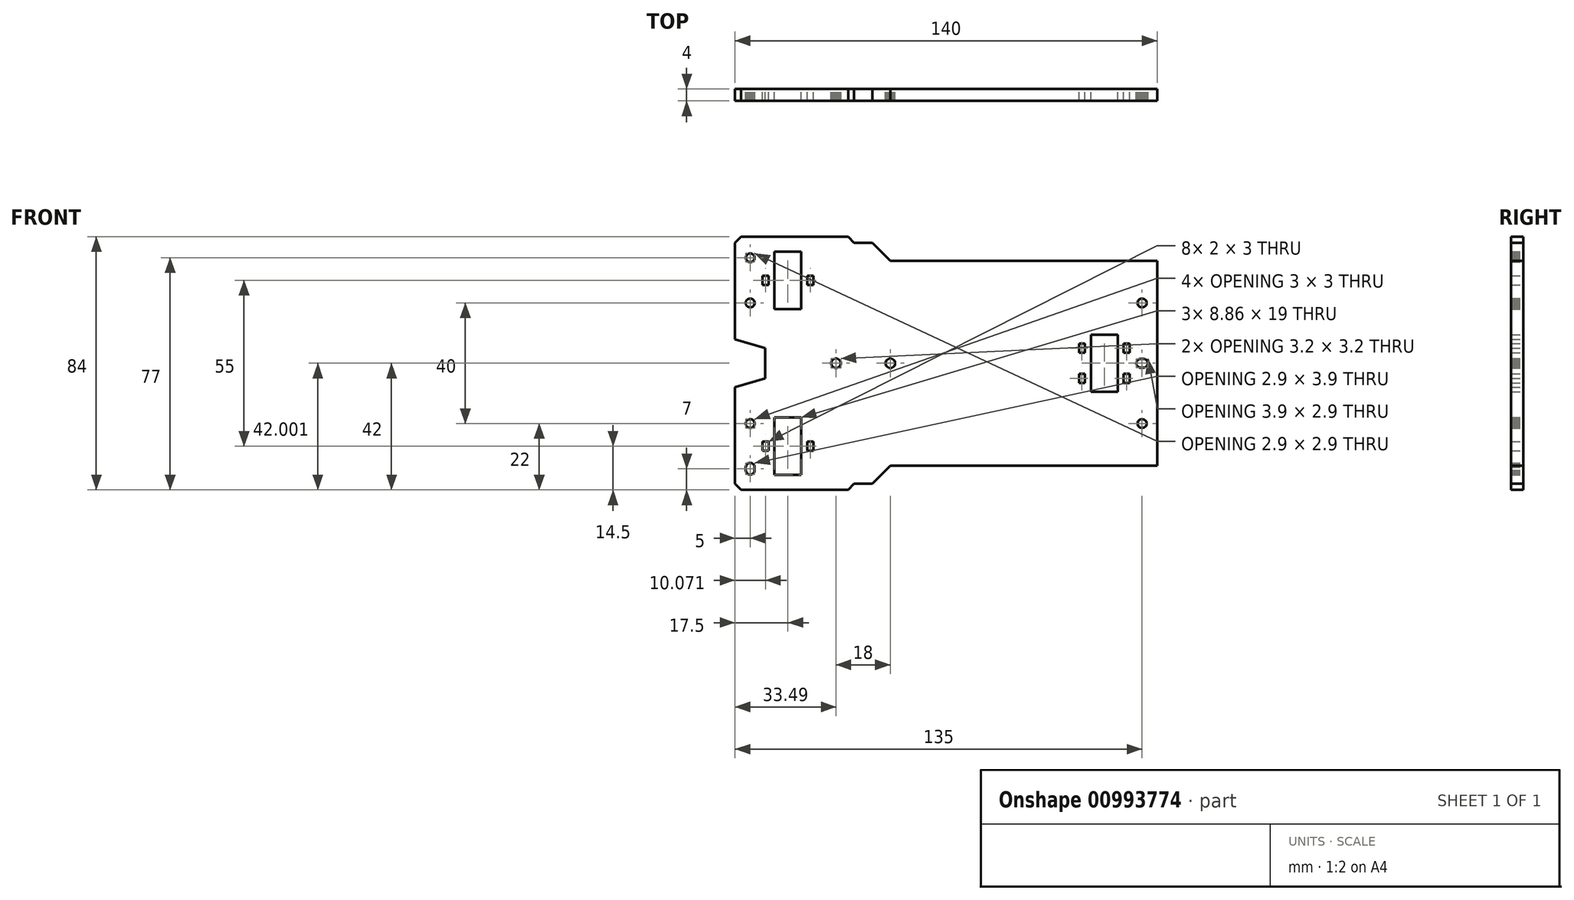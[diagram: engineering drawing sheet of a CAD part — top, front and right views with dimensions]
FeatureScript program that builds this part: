
annotation { "Feature Type Name" : "Feature", "Feature Type Description" : "" }
export const myFeature = defineFeature(function(context is Context, id is Id, definition is map)
    precondition{}
    {
        {
            var Q0;
            Q0=qCreatedBy(makeId("Front.planeOp"),FACE);
            var sketch = newSketch(context, id + "F0", { "sketchPlane" : qUnion([Q0])});
            skLineSegment(sketch, "E0", {"start": v(-65, -33.05) * mm, "end": v(-64.62, -33.1) * mm});
            skLineSegment(sketch, "E1", {"start": v(-64.62, -33.1) * mm, "end": v(-64.28, -33.24) * mm});
            skLineSegment(sketch, "E2", {"start": v(-66.26, -33.77) * mm, "end": v(-66.03, -33.47) * mm});
            skLineSegment(sketch, "E3", {"start": v(-66.03, -33.47) * mm, "end": v(-65.73, -33.24) * mm});
            skLineSegment(sketch, "E4", {"start": v(-66.45, -35.5) * mm, "end": v(-66.45, -34.5) * mm});
            skLineSegment(sketch, "E5", {"start": v(-66.45, -34.5) * mm, "end": v(-66.4, -34.12) * mm});
            skLineSegment(sketch, "E6", {"start": v(-66.4, -34.12) * mm, "end": v(-66.26, -33.77) * mm});
            skLineSegment(sketch, "E7", {"start": v(-65.73, -33.24) * mm, "end": v(-65.38, -33.1) * mm});
            skLineSegment(sketch, "E8", {"start": v(-65.38, -33.1) * mm, "end": v(-65, -33.05) * mm});
            skLineSegment(sketch, "E9", {"start": v(-63.97, -33.47) * mm, "end": v(-63.74, -33.77) * mm});
            skLineSegment(sketch, "E10", {"start": v(63.77, -1.26) * mm, "end": v(63.47, -1.03) * mm});
            skLineSegment(sketch, "E11", {"start": v(-64.28, -33.24) * mm, "end": v(-63.97, -33.47) * mm});
            skLineSegment(sketch, "E12", {"start": v(63.47, -1.03) * mm, "end": v(63.24, -0.73) * mm});
            skLineSegment(sketch, "E13", {"start": v(-63.74, -33.77) * mm, "end": v(-63.6, -34.12) * mm});
            skLineSegment(sketch, "E14", {"start": v(64.5, -1.45) * mm, "end": v(64.12, -1.4) * mm});
            skLineSegment(sketch, "E15", {"start": v(-63.55, -35.5) * mm, "end": v(-63.55, -34.5) * mm});
            skLineSegment(sketch, "E16", {"start": v(-63.6, -34.12) * mm, "end": v(-63.55, -34.5) * mm});
            skLineSegment(sketch, "E17", {"start": v(65.5, -1.45) * mm, "end": v(64.5, -1.45) * mm});
            skLineSegment(sketch, "E18", {"start": v(64.12, -1.4) * mm, "end": v(63.77, -1.26) * mm});
            skLineSegment(sketch, "E19", {"start": v(63.1, -0.38) * mm, "end": v(63.05, 0) * mm});
            skLineSegment(sketch, "E20", {"start": v(63.1, 0.38) * mm, "end": v(63.24, 0.72) * mm});
            skLineSegment(sketch, "E21", {"start": v(63.77, 1.26) * mm, "end": v(64.12, 1.4) * mm});
            skLineSegment(sketch, "E22", {"start": v(64.12, 1.4) * mm, "end": v(64.5, 1.45) * mm});
            skLineSegment(sketch, "E23", {"start": v(65.5, 1.45) * mm, "end": v(64.5, 1.45) * mm});
            skLineSegment(sketch, "E24", {"start": v(63.24, 0.72) * mm, "end": v(63.47, 1.03) * mm});
            skLineSegment(sketch, "E25", {"start": v(63.47, 1.03) * mm, "end": v(63.77, 1.26) * mm});
            skLineSegment(sketch, "E26", {"start": v(63.24, -0.73) * mm, "end": v(63.1, -0.38) * mm});
            skLineSegment(sketch, "E27", {"start": v(63.05, 0) * mm, "end": v(63.1, 0.38) * mm});
            skLineSegment(sketch, "E28", {"start": v(46.07, -6.5) * mm, "end": v(44.07, -6.5) * mm});
            skLineSegment(sketch, "E29", {"start": v(44.07, -6.5) * mm, "end": v(44.07, -3.5) * mm});
            skLineSegment(sketch, "E30", {"start": v(-20.06, 0.41) * mm, "end": v(-20.1, 0) * mm});
            skLineSegment(sketch, "E31", {"start": v(-19.64, 1.13) * mm, "end": v(-19.9, 0.8) * mm});
            skLineSegment(sketch, "E32", {"start": v(-19.3, 1.39) * mm, "end": v(-19.64, 1.13) * mm});
            skLineSegment(sketch, "E33", {"start": v(48.07, -9.5) * mm, "end": v(48.07, 9.5) * mm});
            skLineSegment(sketch, "E34", {"start": v(44.07, -3.5) * mm, "end": v(46.07, -3.5) * mm});
            skLineSegment(sketch, "E35", {"start": v(58.93, -6.5) * mm, "end": v(60.93, -6.5) * mm});
            skLineSegment(sketch, "E36", {"start": v(46.07, -3.5) * mm, "end": v(46.07, -6.5) * mm});
            skLineSegment(sketch, "E37", {"start": v(56.93, -9.5) * mm, "end": v(48.07, -9.5) * mm});
            skLineSegment(sketch, "E38", {"start": v(-18.92, 1.55) * mm, "end": v(-19.3, 1.39) * mm});
            skLineSegment(sketch, "E39", {"start": v(-20.1, 0) * mm, "end": v(-20.06, -0.41) * mm});
            skLineSegment(sketch, "E40", {"start": v(60.93, -6.5) * mm, "end": v(60.93, -3.5) * mm});
            skLineSegment(sketch, "E41", {"start": v(56.93, 9.5) * mm, "end": v(56.93, -9.5) * mm});
            skLineSegment(sketch, "E42", {"start": v(48.07, 9.5) * mm, "end": v(56.93, 9.5) * mm});
            skLineSegment(sketch, "E43", {"start": v(-20.06, -0.41) * mm, "end": v(-19.9, -0.8) * mm});
            skLineSegment(sketch, "E44", {"start": v(-19.9, 0.8) * mm, "end": v(-20.06, 0.41) * mm});
            skLineSegment(sketch, "E45", {"start": v(-16.96, -0.41) * mm, "end": v(-16.9, 0) * mm});
            skLineSegment(sketch, "E46", {"start": v(-17.7, -1.38) * mm, "end": v(-17.38, -1.13) * mm});
            skLineSegment(sketch, "E47", {"start": v(-18.1, -1.54) * mm, "end": v(-17.7, -1.38) * mm});
            skLineSegment(sketch, "E48", {"start": v(-18.5, -1.6) * mm, "end": v(-18.1, -1.54) * mm});
            skLineSegment(sketch, "E49", {"start": v(-18.92, -1.54) * mm, "end": v(-18.5, -1.6) * mm});
            skLineSegment(sketch, "E50", {"start": v(-16.96, 0.41) * mm, "end": v(-17.12, 0.8) * mm});
            skLineSegment(sketch, "E51", {"start": v(-18.5, 1.6) * mm, "end": v(-18.92, 1.55) * mm});
            skLineSegment(sketch, "E52", {"start": v(-17.7, 1.39) * mm, "end": v(-18.1, 1.55) * mm});
            skLineSegment(sketch, "E53", {"start": v(-17.38, 1.13) * mm, "end": v(-17.7, 1.39) * mm});
            skLineSegment(sketch, "E54", {"start": v(-16.9, 0) * mm, "end": v(-16.96, 0.41) * mm});
            skLineSegment(sketch, "E55", {"start": v(-19.3, -1.38) * mm, "end": v(-18.92, -1.54) * mm});
            skLineSegment(sketch, "E56", {"start": v(-18.1, 1.55) * mm, "end": v(-18.5, 1.6) * mm});
            skLineSegment(sketch, "E57", {"start": v(-19.64, -1.13) * mm, "end": v(-19.3, -1.38) * mm});
            skLineSegment(sketch, "E58", {"start": v(-17.12, 0.8) * mm, "end": v(-17.38, 1.13) * mm});
            skLineSegment(sketch, "E59", {"start": v(-17.38, -1.13) * mm, "end": v(-17.12, -0.8) * mm});
            skLineSegment(sketch, "E60", {"start": v(-17.12, -0.8) * mm, "end": v(-16.96, -0.41) * mm});
            skLineSegment(sketch, "E61", {"start": v(-35.38, 1.13) * mm, "end": v(-35.7, 1.39) * mm});
            skLineSegment(sketch, "E62", {"start": v(-38.06, 0.41) * mm, "end": v(-38.1, 0) * mm});
            skLineSegment(sketch, "E63", {"start": v(-37.64, -1.13) * mm, "end": v(-37.3, -1.38) * mm});
            skLineSegment(sketch, "E64", {"start": v(-35.12, 0.8) * mm, "end": v(-35.38, 1.13) * mm});
            skLineSegment(sketch, "E65", {"start": v(-38.1, 0) * mm, "end": v(-38.06, -0.41) * mm});
            skLineSegment(sketch, "E66", {"start": v(-37.9, 0.8) * mm, "end": v(-38.06, 0.41) * mm});
            skLineSegment(sketch, "E67", {"start": v(-37.3, 1.39) * mm, "end": v(-37.64, 1.13) * mm});
            skLineSegment(sketch, "E68", {"start": v(-36.1, 1.55) * mm, "end": v(-36.5, 1.6) * mm});
            skLineSegment(sketch, "E69", {"start": v(-37.64, 1.13) * mm, "end": v(-37.9, 0.8) * mm});
            skLineSegment(sketch, "E70", {"start": v(-37.9, -0.8) * mm, "end": v(-37.64, -1.13) * mm});
            skLineSegment(sketch, "E71", {"start": v(-38.06, -0.41) * mm, "end": v(-37.9, -0.8) * mm});
            skLineSegment(sketch, "E72", {"start": v(-37.3, -1.38) * mm, "end": v(-36.92, -1.54) * mm});
            skLineSegment(sketch, "E73", {"start": v(-36.5, 1.6) * mm, "end": v(-36.92, 1.55) * mm});
            skLineSegment(sketch, "E74", {"start": v(-36.92, 1.55) * mm, "end": v(-37.3, 1.39) * mm});
            skLineSegment(sketch, "E75", {"start": v(-35.7, 1.39) * mm, "end": v(-36.1, 1.55) * mm});
            skLineSegment(sketch, "E76", {"start": v(-19.9, -0.8) * mm, "end": v(-19.64, -1.13) * mm});
            skLineSegment(sketch, "E77", {"start": v(-35.7, -1.38) * mm, "end": v(-35.38, -1.13) * mm});
            skLineSegment(sketch, "E78", {"start": v(-56.93, -37) * mm, "end": v(-48.07, -37) * mm});
            skLineSegment(sketch, "E79", {"start": v(-48.07, 18) * mm, "end": v(-56.93, 18) * mm});
            skLineSegment(sketch, "E80", {"start": v(-56.93, 18) * mm, "end": v(-56.93, 37) * mm});
            skLineSegment(sketch, "E81", {"start": v(-48.07, 37) * mm, "end": v(-48.07, 18) * mm});
            skLineSegment(sketch, "E82", {"start": v(-35.12, -0.8) * mm, "end": v(-34.96, -0.41) * mm});
            skLineSegment(sketch, "E83", {"start": v(-34.96, -0.41) * mm, "end": v(-34.9, 0) * mm});
            skLineSegment(sketch, "E84", {"start": v(-36.1, -1.54) * mm, "end": v(-35.7, -1.38) * mm});
            skLineSegment(sketch, "E85", {"start": v(-34.9, 0) * mm, "end": v(-34.96, 0.41) * mm});
            skLineSegment(sketch, "E86", {"start": v(-35.38, -1.13) * mm, "end": v(-35.12, -0.8) * mm});
            skLineSegment(sketch, "E87", {"start": v(-56.93, -18) * mm, "end": v(-56.93, -37) * mm});
            skLineSegment(sketch, "E88", {"start": v(-48.07, -37) * mm, "end": v(-48.07, -18) * mm});
            skLineSegment(sketch, "E89", {"start": v(-36.5, -1.6) * mm, "end": v(-36.1, -1.54) * mm});
            skLineSegment(sketch, "E90", {"start": v(-36.92, -1.54) * mm, "end": v(-36.5, -1.6) * mm});
            skLineSegment(sketch, "E91", {"start": v(-48.07, -18) * mm, "end": v(-56.93, -18) * mm});
            skLineSegment(sketch, "E92", {"start": v(-34.96, 0.41) * mm, "end": v(-35.12, 0.8) * mm});
            skLineSegment(sketch, "E93", {"start": v(-44.07, -29) * mm, "end": v(-44.07, -26) * mm});
            skLineSegment(sketch, "E94", {"start": v(-46.07, -26) * mm, "end": v(-46.07, -29) * mm});
            skLineSegment(sketch, "E95", {"start": v(-46.07, -29) * mm, "end": v(-44.07, -29) * mm});
            skLineSegment(sketch, "E96", {"start": v(-58.93, 26) * mm, "end": v(-60.93, 26) * mm});
            skLineSegment(sketch, "E97", {"start": v(-60.93, 26) * mm, "end": v(-60.93, 29) * mm});
            skLineSegment(sketch, "E98", {"start": v(-44.07, -26) * mm, "end": v(-46.07, -26) * mm});
            skLineSegment(sketch, "E99", {"start": v(-58.93, -29) * mm, "end": v(-60.93, -29) * mm});
            skLineSegment(sketch, "E100", {"start": v(-60.93, -29) * mm, "end": v(-60.93, -26) * mm});
            skLineSegment(sketch, "E101", {"start": v(-44.07, 26) * mm, "end": v(-44.07, 29) * mm});
            skLineSegment(sketch, "E102", {"start": v(-46.07, 29) * mm, "end": v(-46.07, 26) * mm});
            skLineSegment(sketch, "E103", {"start": v(-60.93, -26) * mm, "end": v(-58.93, -26) * mm});
            skLineSegment(sketch, "E104", {"start": v(-58.93, -26) * mm, "end": v(-58.93, -29) * mm});
            skLineSegment(sketch, "E105", {"start": v(-44.07, 29) * mm, "end": v(-46.07, 29) * mm});
            skLineSegment(sketch, "E106", {"start": v(-46.07, 26) * mm, "end": v(-44.07, 26) * mm});
            skLineSegment(sketch, "E107", {"start": v(-58.93, 29) * mm, "end": v(-58.93, 26) * mm});
            skLineSegment(sketch, "E108", {"start": v(-56.93, 37) * mm, "end": v(-48.07, 37) * mm});
            skLineSegment(sketch, "E109", {"start": v(-30.5, 12) * mm, "end": v(-30.5, 6) * mm});
            skLineSegment(sketch, "E110", {"start": v(-30.5, -18) * mm, "end": v(-24.5, -18) * mm});
            skLineSegment(sketch, "E111", {"start": v(-30.5, 24) * mm, "end": v(-30.5, 18) * mm});
            skLineSegment(sketch, "E112", {"start": v(-24.5, 6) * mm, "end": v(-24.5, 12) * mm});
            skLineSegment(sketch, "E113", {"start": v(-24.5, -6) * mm, "end": v(-24.5, -12) * mm});
            skLineSegment(sketch, "E114", {"start": v(-24.5, 24) * mm, "end": v(-30.5, 24) * mm});
            skLineSegment(sketch, "E115", {"start": v(-30.5, 6) * mm, "end": v(-24.5, 6) * mm});
            skLineSegment(sketch, "E116", {"start": v(-24.5, 12) * mm, "end": v(-30.5, 12) * mm});
            skLineSegment(sketch, "E117", {"start": v(-30.5, -6) * mm, "end": v(-24.5, -6) * mm});
            skLineSegment(sketch, "E118", {"start": v(-24.5, -12) * mm, "end": v(-30.5, -12) * mm});
            skLineSegment(sketch, "E119", {"start": v(-30.5, 18) * mm, "end": v(-24.5, 18) * mm});
            skLineSegment(sketch, "E120", {"start": v(-60.93, 29) * mm, "end": v(-58.93, 29) * mm});
            skLineSegment(sketch, "E121", {"start": v(-24.5, -18) * mm, "end": v(-24.5, -24) * mm});
            skLineSegment(sketch, "E122", {"start": v(-24.5, 18) * mm, "end": v(-24.5, 24) * mm});
            skLineSegment(sketch, "E123", {"start": v(-30.5, -12) * mm, "end": v(-30.5, -6) * mm});
            skLineSegment(sketch, "E124", {"start": v(-24.5, -24) * mm, "end": v(-30.5, -24) * mm});
            skLineSegment(sketch, "E125", {"start": v(-30.5, -24) * mm, "end": v(-30.5, -18) * mm});
            skLineSegment(sketch, "E126", {"start": v(63.7, 20.75) * mm, "end": v(63.94, 21.06) * mm});
            skLineSegment(sketch, "E127", {"start": v(63.55, 20.39) * mm, "end": v(63.7, 20.75) * mm});
            skLineSegment(sketch, "E128", {"start": v(63.94, 21.06) * mm, "end": v(64.25, 21.3) * mm});
            skLineSegment(sketch, "E129", {"start": v(65.39, 21.45) * mm, "end": v(65.75, 21.3) * mm});
            skLineSegment(sketch, "E130", {"start": v(63.5, 20) * mm, "end": v(63.55, 20.39) * mm});
            skLineSegment(sketch, "E131", {"start": v(64.25, 21.3) * mm, "end": v(64.61, 21.45) * mm});
            skLineSegment(sketch, "E132", {"start": v(64.61, 21.45) * mm, "end": v(65, 21.5) * mm});
            skLineSegment(sketch, "E133", {"start": v(65, 21.5) * mm, "end": v(65.39, 21.45) * mm});
            skLineSegment(sketch, "E134", {"start": v(65.75, 21.3) * mm, "end": v(66.06, 21.06) * mm});
            skLineSegment(sketch, "E135", {"start": v(66.06, 21.06) * mm, "end": v(66.3, 20.75) * mm});
            skLineSegment(sketch, "E136", {"start": v(63.55, 19.61) * mm, "end": v(63.5, 20) * mm});
            skLineSegment(sketch, "E137", {"start": v(-70, 40) * mm, "end": v(-70, 8) * mm});
            skLineSegment(sketch, "E138", {"start": v(-60, 5) * mm, "end": v(-70, 8) * mm});
            skLineSegment(sketch, "E139", {"start": v(-60, -5) * mm, "end": v(-60, 5) * mm});
            skLineSegment(sketch, "E140", {"start": v(-70, -8) * mm, "end": v(-60, -5) * mm});
            skLineSegment(sketch, "E141", {"start": v(-70, -8) * mm, "end": v(-70, -40) * mm});
            skLineSegment(sketch, "E142", {"start": v(-70, -40) * mm, "end": v(-68, -42) * mm});
            skLineSegment(sketch, "E143", {"start": v(-68, -42) * mm, "end": v(-32.5, -42) * mm});
            skLineSegment(sketch, "E144", {"start": v(-30.5, -40) * mm, "end": v(-32.5, -42) * mm});
            skLineSegment(sketch, "E145", {"start": v(-30.5, -40) * mm, "end": v(-24.5, -40) * mm});
            skLineSegment(sketch, "E146", {"start": v(-24.5, -40) * mm, "end": v(-18.5, -34) * mm});
            skLineSegment(sketch, "E147", {"start": v(-18.5, -34) * mm, "end": v(70, -34) * mm});
            skLineSegment(sketch, "E148", {"start": v(70, -34) * mm, "end": v(70, 34) * mm});
            skLineSegment(sketch, "E149", {"start": v(-18.5, 34) * mm, "end": v(70, 34) * mm});
            skLineSegment(sketch, "E150", {"start": v(-24.5, 40) * mm, "end": v(-18.5, 34) * mm});
            skLineSegment(sketch, "E151", {"start": v(-24.5, 40) * mm, "end": v(-30.5, 40) * mm});
            skLineSegment(sketch, "E152", {"start": v(-30.5, 40) * mm, "end": v(-32.5, 42) * mm});
            skLineSegment(sketch, "E153", {"start": v(-32.5, 42) * mm, "end": v(-68, 42) * mm});
            skLineSegment(sketch, "E154", {"start": v(-70, 40) * mm, "end": v(-68, 42) * mm});
            skLineSegment(sketch, "E155", {"start": v(-63.7, 19.25) * mm, "end": v(-63.94, 18.94) * mm});
            skLineSegment(sketch, "E156", {"start": v(-63.94, 18.94) * mm, "end": v(-64.25, 18.7) * mm});
            skLineSegment(sketch, "E157", {"start": v(-64.25, 18.7) * mm, "end": v(-64.61, 18.55) * mm});
            skLineSegment(sketch, "E158", {"start": v(-64.61, 18.55) * mm, "end": v(-65, 18.5) * mm});
            skLineSegment(sketch, "E159", {"start": v(-65, 18.5) * mm, "end": v(-65.39, 18.55) * mm});
            skLineSegment(sketch, "E160", {"start": v(-65.39, 18.55) * mm, "end": v(-65.75, 18.7) * mm});
            skLineSegment(sketch, "E161", {"start": v(-65.75, 18.7) * mm, "end": v(-66.06, 18.94) * mm});
            skLineSegment(sketch, "E162", {"start": v(-66.06, 18.94) * mm, "end": v(-66.3, 19.25) * mm});
            skLineSegment(sketch, "E163", {"start": v(-66.3, 19.25) * mm, "end": v(-66.45, 19.61) * mm});
            skLineSegment(sketch, "E164", {"start": v(-66.45, 19.61) * mm, "end": v(-66.5, 20) * mm});
            skLineSegment(sketch, "E165", {"start": v(-66.5, 20) * mm, "end": v(-66.45, 20.39) * mm});
            skLineSegment(sketch, "E166", {"start": v(-66.45, 20.39) * mm, "end": v(-66.3, 20.75) * mm});
            skLineSegment(sketch, "E167", {"start": v(-66.3, 20.75) * mm, "end": v(-66.06, 21.06) * mm});
            skLineSegment(sketch, "E168", {"start": v(-66.06, 21.06) * mm, "end": v(-65.75, 21.3) * mm});
            skLineSegment(sketch, "E169", {"start": v(-65.75, 21.3) * mm, "end": v(-65.39, 21.45) * mm});
            skLineSegment(sketch, "E170", {"start": v(-65.39, 21.45) * mm, "end": v(-65, 21.5) * mm});
            skLineSegment(sketch, "E171", {"start": v(-65, 21.5) * mm, "end": v(-64.61, 21.45) * mm});
            skLineSegment(sketch, "E172", {"start": v(-64.61, 21.45) * mm, "end": v(-64.25, 21.3) * mm});
            skLineSegment(sketch, "E173", {"start": v(-64.25, 21.3) * mm, "end": v(-63.94, 21.06) * mm});
            skLineSegment(sketch, "E174", {"start": v(-63.94, 21.06) * mm, "end": v(-63.7, 20.75) * mm});
            skLineSegment(sketch, "E175", {"start": v(-63.7, 20.75) * mm, "end": v(-63.55, 20.39) * mm});
            skLineSegment(sketch, "E176", {"start": v(-63.55, 20.39) * mm, "end": v(-63.5, 20) * mm});
            skLineSegment(sketch, "E177", {"start": v(-63.5, 20) * mm, "end": v(-63.55, 19.61) * mm});
            skLineSegment(sketch, "E178", {"start": v(-63.55, 19.61) * mm, "end": v(-63.7, 19.25) * mm});
            skLineSegment(sketch, "E179", {"start": v(-66.3, -19.25) * mm, "end": v(-66.06, -18.94) * mm});
            skLineSegment(sketch, "E180", {"start": v(-66.06, -18.94) * mm, "end": v(-65.75, -18.7) * mm});
            skLineSegment(sketch, "E181", {"start": v(-65.75, -18.7) * mm, "end": v(-65.39, -18.55) * mm});
            skLineSegment(sketch, "E182", {"start": v(-65.39, -18.55) * mm, "end": v(-65, -18.5) * mm});
            skLineSegment(sketch, "E183", {"start": v(-65, -18.5) * mm, "end": v(-64.61, -18.55) * mm});
            skLineSegment(sketch, "E184", {"start": v(-64.61, -18.55) * mm, "end": v(-64.25, -18.7) * mm});
            skLineSegment(sketch, "E185", {"start": v(-64.25, -18.7) * mm, "end": v(-63.94, -18.94) * mm});
            skLineSegment(sketch, "E186", {"start": v(-63.94, -18.94) * mm, "end": v(-63.7, -19.25) * mm});
            skLineSegment(sketch, "E187", {"start": v(-63.7, -19.25) * mm, "end": v(-63.55, -19.61) * mm});
            skLineSegment(sketch, "E188", {"start": v(-63.55, -19.61) * mm, "end": v(-63.5, -20) * mm});
            skLineSegment(sketch, "E189", {"start": v(-63.5, -20) * mm, "end": v(-63.55, -20.39) * mm});
            skLineSegment(sketch, "E190", {"start": v(-63.55, -20.39) * mm, "end": v(-63.7, -20.75) * mm});
            skLineSegment(sketch, "E191", {"start": v(-63.7, -20.75) * mm, "end": v(-63.94, -21.06) * mm});
            skLineSegment(sketch, "E192", {"start": v(-63.94, -21.06) * mm, "end": v(-64.25, -21.3) * mm});
            skLineSegment(sketch, "E193", {"start": v(-64.25, -21.3) * mm, "end": v(-64.61, -21.45) * mm});
            skLineSegment(sketch, "E194", {"start": v(-64.61, -21.45) * mm, "end": v(-65, -21.5) * mm});
            skLineSegment(sketch, "E195", {"start": v(-65, -21.5) * mm, "end": v(-65.39, -21.45) * mm});
            skLineSegment(sketch, "E196", {"start": v(-65.39, -21.45) * mm, "end": v(-65.75, -21.3) * mm});
            skLineSegment(sketch, "E197", {"start": v(-65.75, -21.3) * mm, "end": v(-66.06, -21.06) * mm});
            skLineSegment(sketch, "E198", {"start": v(-66.06, -21.06) * mm, "end": v(-66.3, -20.75) * mm});
            skLineSegment(sketch, "E199", {"start": v(-66.3, -20.75) * mm, "end": v(-66.45, -20.39) * mm});
            skLineSegment(sketch, "E200", {"start": v(-66.45, -20.39) * mm, "end": v(-66.5, -20) * mm});
            skLineSegment(sketch, "E201", {"start": v(-66.5, -20) * mm, "end": v(-66.45, -19.61) * mm});
            skLineSegment(sketch, "E202", {"start": v(-66.45, -19.61) * mm, "end": v(-66.3, -19.25) * mm});
            skLineSegment(sketch, "E203", {"start": v(66.3, 20.75) * mm, "end": v(66.45, 20.39) * mm});
            skLineSegment(sketch, "E204", {"start": v(66.45, 20.39) * mm, "end": v(66.5, 20) * mm});
            skLineSegment(sketch, "E205", {"start": v(66.5, 20) * mm, "end": v(66.45, 19.61) * mm});
            skLineSegment(sketch, "E206", {"start": v(66.45, 19.61) * mm, "end": v(66.3, 19.25) * mm});
            skLineSegment(sketch, "E207", {"start": v(66.3, 19.25) * mm, "end": v(66.06, 18.94) * mm});
            skLineSegment(sketch, "E208", {"start": v(66.06, 18.94) * mm, "end": v(65.75, 18.7) * mm});
            skLineSegment(sketch, "E209", {"start": v(65.75, 18.7) * mm, "end": v(65.39, 18.55) * mm});
            skLineSegment(sketch, "E210", {"start": v(65.39, 18.55) * mm, "end": v(65, 18.5) * mm});
            skLineSegment(sketch, "E211", {"start": v(65, 18.5) * mm, "end": v(64.61, 18.55) * mm});
            skLineSegment(sketch, "E212", {"start": v(64.61, 18.55) * mm, "end": v(64.25, 18.7) * mm});
            skLineSegment(sketch, "E213", {"start": v(64.25, 18.7) * mm, "end": v(63.94, 18.94) * mm});
            skLineSegment(sketch, "E214", {"start": v(63.94, 18.94) * mm, "end": v(63.7, 19.25) * mm});
            skLineSegment(sketch, "E215", {"start": v(63.7, 19.25) * mm, "end": v(63.55, 19.61) * mm});
            skLineSegment(sketch, "E216", {"start": v(65.39, -21.45) * mm, "end": v(65, -21.5) * mm});
            skLineSegment(sketch, "E217", {"start": v(65, -21.5) * mm, "end": v(64.61, -21.45) * mm});
            skLineSegment(sketch, "E218", {"start": v(64.61, -21.45) * mm, "end": v(64.25, -21.3) * mm});
            skLineSegment(sketch, "E219", {"start": v(64.25, -21.3) * mm, "end": v(63.94, -21.06) * mm});
            skLineSegment(sketch, "E220", {"start": v(63.94, -21.06) * mm, "end": v(63.7, -20.75) * mm});
            skLineSegment(sketch, "E221", {"start": v(63.7, -20.75) * mm, "end": v(63.55, -20.39) * mm});
            skLineSegment(sketch, "E222", {"start": v(63.55, -20.39) * mm, "end": v(63.5, -20) * mm});
            skLineSegment(sketch, "E223", {"start": v(63.5, -20) * mm, "end": v(63.55, -19.61) * mm});
            skLineSegment(sketch, "E224", {"start": v(63.55, -19.61) * mm, "end": v(63.7, -19.25) * mm});
            skLineSegment(sketch, "E225", {"start": v(63.7, -19.25) * mm, "end": v(63.94, -18.94) * mm});
            skLineSegment(sketch, "E226", {"start": v(63.94, -18.94) * mm, "end": v(64.25, -18.7) * mm});
            skLineSegment(sketch, "E227", {"start": v(64.25, -18.7) * mm, "end": v(64.61, -18.55) * mm});
            skLineSegment(sketch, "E228", {"start": v(64.61, -18.55) * mm, "end": v(65, -18.5) * mm});
            skLineSegment(sketch, "E229", {"start": v(65, -18.5) * mm, "end": v(65.39, -18.55) * mm});
            skLineSegment(sketch, "E230", {"start": v(65.39, -18.55) * mm, "end": v(65.75, -18.7) * mm});
            skLineSegment(sketch, "E231", {"start": v(65.75, -18.7) * mm, "end": v(66.06, -18.94) * mm});
            skLineSegment(sketch, "E232", {"start": v(66.06, -18.94) * mm, "end": v(66.3, -19.25) * mm});
            skLineSegment(sketch, "E233", {"start": v(66.3, -19.25) * mm, "end": v(66.45, -19.61) * mm});
            skLineSegment(sketch, "E234", {"start": v(66.45, -19.61) * mm, "end": v(66.5, -20) * mm});
            skLineSegment(sketch, "E235", {"start": v(66.5, -20) * mm, "end": v(66.45, -20.39) * mm});
            skLineSegment(sketch, "E236", {"start": v(66.45, -20.39) * mm, "end": v(66.3, -20.75) * mm});
            skLineSegment(sketch, "E237", {"start": v(66.3, -20.75) * mm, "end": v(66.06, -21.06) * mm});
            skLineSegment(sketch, "E238", {"start": v(66.06, -21.06) * mm, "end": v(65.75, -21.3) * mm});
            skLineSegment(sketch, "E239", {"start": v(65.75, -21.3) * mm, "end": v(65.39, -21.45) * mm});
            skLineSegment(sketch, "E240", {"start": v(-66.4, -35.88) * mm, "end": v(-66.45, -35.5) * mm});
            skLineSegment(sketch, "E241", {"start": v(-63.55, -35.5) * mm, "end": v(-63.6, -35.88) * mm});
            skLineSegment(sketch, "E242", {"start": v(-63.6, -35.88) * mm, "end": v(-63.74, -36.22) * mm});
            skLineSegment(sketch, "E243", {"start": v(-63.74, -36.22) * mm, "end": v(-63.97, -36.53) * mm});
            skLineSegment(sketch, "E244", {"start": v(-63.97, -36.53) * mm, "end": v(-64.28, -36.76) * mm});
            skLineSegment(sketch, "E245", {"start": v(-64.28, -36.76) * mm, "end": v(-64.62, -36.9) * mm});
            skLineSegment(sketch, "E246", {"start": v(-64.62, -36.9) * mm, "end": v(-65, -36.95) * mm});
            skLineSegment(sketch, "E247", {"start": v(-65, -36.95) * mm, "end": v(-65.38, -36.9) * mm});
            skLineSegment(sketch, "E248", {"start": v(-65.38, -36.9) * mm, "end": v(-65.73, -36.76) * mm});
            skLineSegment(sketch, "E249", {"start": v(-65.73, -36.76) * mm, "end": v(-66.03, -36.53) * mm});
            skLineSegment(sketch, "E250", {"start": v(-66.03, -36.53) * mm, "end": v(-66.26, -36.22) * mm});
            skLineSegment(sketch, "E251", {"start": v(-66.26, -36.22) * mm, "end": v(-66.4, -35.88) * mm});
            skLineSegment(sketch, "E252", {"start": v(65.88, -1.4) * mm, "end": v(65.5, -1.45) * mm});
            skLineSegment(sketch, "E253", {"start": v(65.5, 1.45) * mm, "end": v(65.88, 1.4) * mm});
            skLineSegment(sketch, "E254", {"start": v(65.88, 1.4) * mm, "end": v(66.22, 1.26) * mm});
            skLineSegment(sketch, "E255", {"start": v(66.22, 1.26) * mm, "end": v(66.53, 1.03) * mm});
            skLineSegment(sketch, "E256", {"start": v(66.53, 1.03) * mm, "end": v(66.76, 0.72) * mm});
            skLineSegment(sketch, "E257", {"start": v(66.76, 0.72) * mm, "end": v(66.9, 0.38) * mm});
            skLineSegment(sketch, "E258", {"start": v(66.9, 0.38) * mm, "end": v(66.95, 0) * mm});
            skLineSegment(sketch, "E259", {"start": v(66.95, 0) * mm, "end": v(66.9, -0.38) * mm});
            skLineSegment(sketch, "E260", {"start": v(66.9, -0.38) * mm, "end": v(66.76, -0.73) * mm});
            skLineSegment(sketch, "E261", {"start": v(66.76, -0.73) * mm, "end": v(66.53, -1.03) * mm});
            skLineSegment(sketch, "E262", {"start": v(66.53, -1.03) * mm, "end": v(66.22, -1.26) * mm});
            skLineSegment(sketch, "E263", {"start": v(66.22, -1.26) * mm, "end": v(65.88, -1.4) * mm});
            skLineSegment(sketch, "E264", {"start": v(-65.72, 36.26) * mm, "end": v(-65.38, 36.4) * mm});
            skLineSegment(sketch, "E265", {"start": v(-65.38, 36.4) * mm, "end": v(-65, 36.45) * mm});
            skLineSegment(sketch, "E266", {"start": v(-65, 36.45) * mm, "end": v(-64.62, 36.4) * mm});
            skLineSegment(sketch, "E267", {"start": v(-64.62, 36.4) * mm, "end": v(-64.28, 36.26) * mm});
            skLineSegment(sketch, "E268", {"start": v(-64.28, 36.26) * mm, "end": v(-63.97, 36.03) * mm});
            skLineSegment(sketch, "E269", {"start": v(-63.97, 36.03) * mm, "end": v(-63.74, 35.73) * mm});
            skLineSegment(sketch, "E270", {"start": v(-63.74, 35.73) * mm, "end": v(-63.6, 35.38) * mm});
            skLineSegment(sketch, "E271", {"start": v(-63.6, 35.38) * mm, "end": v(-63.55, 35) * mm});
            skLineSegment(sketch, "E272", {"start": v(-63.55, 35) * mm, "end": v(-63.6, 34.62) * mm});
            skLineSegment(sketch, "E273", {"start": v(-63.6, 34.62) * mm, "end": v(-63.74, 34.28) * mm});
            skLineSegment(sketch, "E274", {"start": v(-63.74, 34.28) * mm, "end": v(-63.97, 33.97) * mm});
            skLineSegment(sketch, "E275", {"start": v(-63.97, 33.97) * mm, "end": v(-64.28, 33.74) * mm});
            skLineSegment(sketch, "E276", {"start": v(-64.28, 33.74) * mm, "end": v(-64.62, 33.6) * mm});
            skLineSegment(sketch, "E277", {"start": v(-64.62, 33.6) * mm, "end": v(-65, 33.55) * mm});
            skLineSegment(sketch, "E278", {"start": v(-65, 33.55) * mm, "end": v(-65.38, 33.6) * mm});
            skLineSegment(sketch, "E279", {"start": v(-65.38, 33.6) * mm, "end": v(-65.72, 33.74) * mm});
            skLineSegment(sketch, "E280", {"start": v(-65.72, 33.74) * mm, "end": v(-66.03, 33.97) * mm});
            skLineSegment(sketch, "E281", {"start": v(-66.03, 33.97) * mm, "end": v(-66.26, 34.28) * mm});
            skLineSegment(sketch, "E282", {"start": v(-66.26, 34.28) * mm, "end": v(-66.4, 34.62) * mm});
            skLineSegment(sketch, "E283", {"start": v(-66.4, 34.62) * mm, "end": v(-66.45, 35) * mm});
            skLineSegment(sketch, "E284", {"start": v(-66.45, 35) * mm, "end": v(-66.4, 35.38) * mm});
            skLineSegment(sketch, "E285", {"start": v(-66.4, 35.38) * mm, "end": v(-66.26, 35.73) * mm});
            skLineSegment(sketch, "E286", {"start": v(-66.26, 35.73) * mm, "end": v(-66.03, 36.03) * mm});
            skLineSegment(sketch, "E287", {"start": v(-66.03, 36.03) * mm, "end": v(-65.72, 36.26) * mm});
            skLineSegment(sketch, "E288", {"start": v(58.93, 3.5) * mm, "end": v(58.93, 6.5) * mm});
            skLineSegment(sketch, "E289", {"start": v(60.93, 6.5) * mm, "end": v(58.93, 6.5) * mm});
            skLineSegment(sketch, "E290", {"start": v(60.93, 6.5) * mm, "end": v(60.93, 3.5) * mm});
            skLineSegment(sketch, "E291", {"start": v(58.93, 3.5) * mm, "end": v(60.93, 3.5) * mm});
            skLineSegment(sketch, "E292", {"start": v(44.07, 3.5) * mm, "end": v(44.07, 6.5) * mm});
            skLineSegment(sketch, "E293", {"start": v(44.07, 6.5) * mm, "end": v(46.07, 6.5) * mm});
            skLineSegment(sketch, "E294", {"start": v(46.07, 6.5) * mm, "end": v(46.07, 3.5) * mm});
            skLineSegment(sketch, "E295", {"start": v(46.07, 3.5) * mm, "end": v(44.07, 3.5) * mm});
            skLineSegment(sketch, "E296", {"start": v(58.93, -3.5) * mm, "end": v(58.93, -6.5) * mm});
            skLineSegment(sketch, "E297", {"start": v(60.93, -3.5) * mm, "end": v(58.93, -3.5) * mm});
            skSolve(sketch);
        }
        {
            var Q0;
            Q0=makeQuery(id+"F0.imprint","IMPRINT",FACE,{"disambiguationData":[TD([[makeQuery(id+"F0.imprint","IMPRINT",EDGE,{"derivedFrom":sQuery(id+"F0.wireOp",EDGE,"E0")}),1.0]])]});
            var Q1;
            Q1=makeQuery(id+"F0.imprint","IMPRINT",FACE,{"disambiguationData":[TD([[makeQuery(id+"F0.imprint","IMPRINT",EDGE,{"derivedFrom":sQuery(id+"F0.wireOp",EDGE,"E111")}),1.0]])]});
            var Q2;
            Q2=makeQuery(id+"F0.imprint","IMPRINT",FACE,{"disambiguationData":[TD([[makeQuery(id+"F0.imprint","IMPRINT",EDGE,{"derivedFrom":sQuery(id+"F0.wireOp",EDGE,"E109")}),1.0]])]});
            var Q3;
            Q3=makeQuery(id+"F0.imprint","IMPRINT",FACE,{"disambiguationData":[TD([[makeQuery(id+"F0.imprint","IMPRINT",EDGE,{"derivedFrom":sQuery(id+"F0.wireOp",EDGE,"E113")}),-1.0]])]});
            var Q4;
            Q4=makeQuery(id+"F0.imprint","IMPRINT",FACE,{"disambiguationData":[TD([[makeQuery(id+"F0.imprint","IMPRINT",EDGE,{"derivedFrom":sQuery(id+"F0.wireOp",EDGE,"E110")}),-1.0]])]});
            extrude(context, id + "F1", {"entities" : qUnion([Q0, Q1, Q2, Q3, Q4]), "depth" : 4 * mm, "offsetDistance" : 25 * mm});
        }
    });
